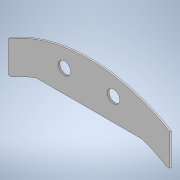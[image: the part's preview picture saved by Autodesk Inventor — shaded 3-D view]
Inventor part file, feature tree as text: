
AUTODESK INVENTOR PART (.ipt)
format: ipt  version: 2021 (Build 250183000, 183)  size: 106,496 bytes
history: native  units: mm
features: extrude x1, sketch x1
ambient origin geometry x8: Origin, YZ Plane, XZ Plane, XY Plane, X Axis, Y Axis, Z Axis, Center Point
bodies: Solid1 (feature_tree)
feature tree (2):
  extrude  "Extrusion1"  [1 undecoded]
  sketch  "Sketch1"  dims[d0=0.5mm d1=0.0mm]
note: 1 required parameter value undecoded (feature->parameter linkage not recoverable at this tier; creation-order binding heuristic only, values carry confidence <= 0.55)
